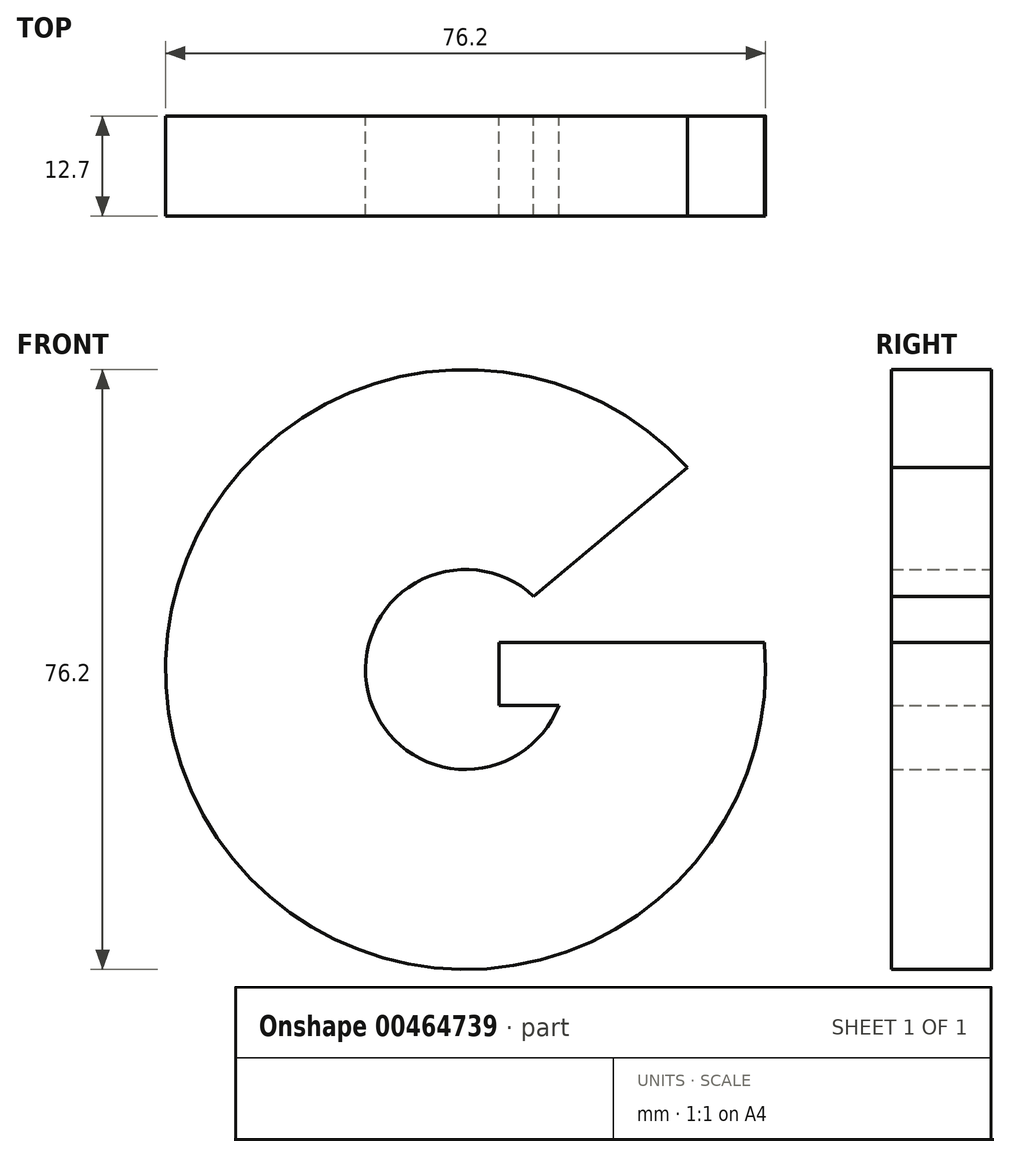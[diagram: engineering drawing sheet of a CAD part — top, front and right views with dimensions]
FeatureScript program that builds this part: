
annotation { "Feature Type Name" : "Feature", "Feature Type Description" : "" }
export const myFeature = defineFeature(function(context is Context, id is Id, definition is map)
    precondition{}
    {
        {
            var Q0;
            Q0=qCreatedBy(makeId("Front.planeOp"),FACE);
            var sketch = newSketch(context, id + "F0", { "sketchPlane" : qUnion([Q0])});
            skArc(sketch, "E0", {"start": v(28.17, 25.65) * mm, "mid": v(-34.87, -15.34) * mm, "end": v(37.94, 3.44) * mm});
            skArc(sketch, "E1", {"start": v(8.65, 9.3) * mm, "mid": v(-12.38, -2.84) * mm, "end": v(11.84, -4.6) * mm});
            skLineSegment(sketch, "E2", {"start": v(8.16, 8.9) * mm, "end": v(28.17, 25.65) * mm});
            skLineSegment(sketch, "E3", {"start": v(12.23, 3.44) * mm, "end": v(37.94, 3.44) * mm});
            skLineSegment(sketch, "E4", {"start": v(11.84, -4.6) * mm, "end": v(4.22, -4.6) * mm});
            skLineSegment(sketch, "E5", {"start": v(4.22, -4.6) * mm, "end": v(4.22, 6.85) * mm});
            skLineSegment(sketch, "E6", {"start": v(12.23, 3.44) * mm, "end": v(4.22, 3.44) * mm});
            skSolve(sketch);
        }
        {
            var Q0;
            {var subQ1=sQuery(id+"F0.wireOp",EDGE,"E0");Q0=makeQuery(id+"F0.imprint","IMPRINT",FACE,{"disambiguationData":[TD([[makeQuery(id+"F0.imprint","IMPRINT",EDGE,{"derivedFrom":subQ1}),1.0]])]});}
            extrude(context, id + "F1", {"entities" : qUnion([Q0]), "depth" : 12.7 * mm});
        }
    });
